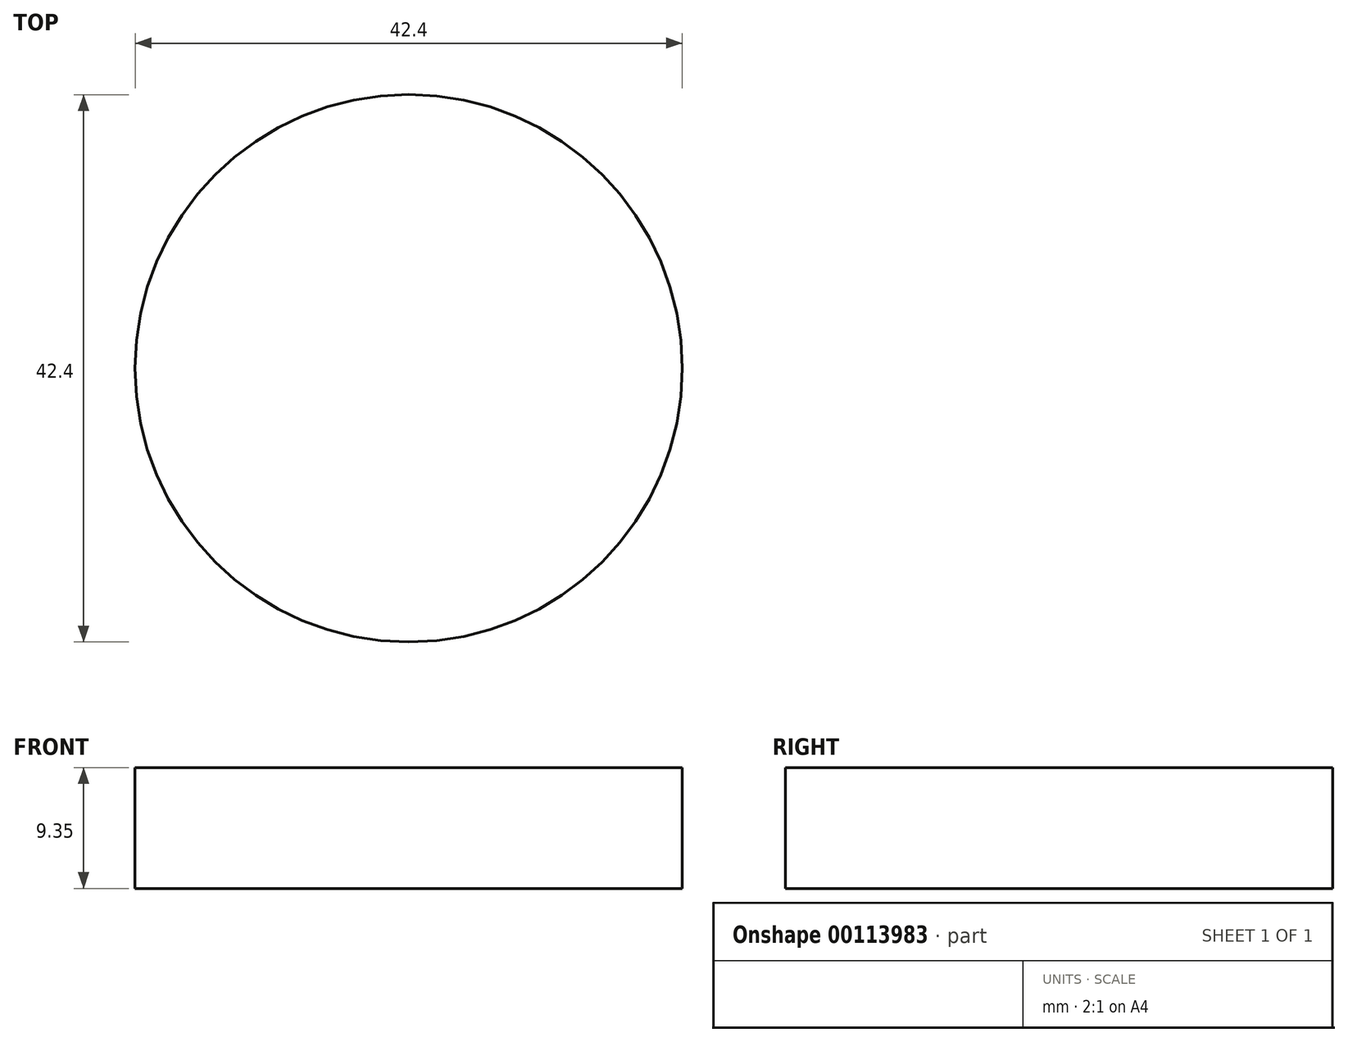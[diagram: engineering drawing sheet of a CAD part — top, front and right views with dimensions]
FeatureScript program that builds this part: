
annotation { "Feature Type Name" : "Feature", "Feature Type Description" : "" }
export const myFeature = defineFeature(function(context is Context, id is Id, definition is map)
    precondition{}
    {
        {
            var Q0;
            Q0=qCreatedBy(makeId("Top.planeOp"),FACE);
            var sketch = newSketch(context, id + "F0", { "sketchPlane" : qUnion([Q0])});
            skCircle(sketch, "E0", {"center": v(0, 0) * mm, "radius": 21.2 * mm});
            skSolve(sketch);
        }
        {
            var Q0;
            Q0 = qSketchRegion(id + "F0", true);
            extrude(context, id + "F1", {"entities" : qUnion([Q0]), "depth" : 9.35 * mm});
        }
    });
